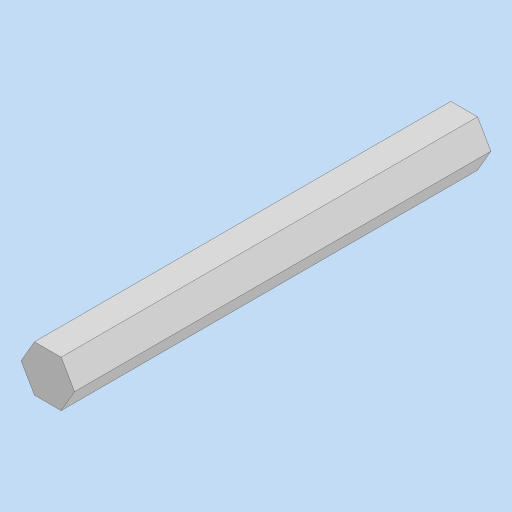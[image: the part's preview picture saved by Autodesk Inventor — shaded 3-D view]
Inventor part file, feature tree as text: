
AUTODESK INVENTOR PART (.ipt)
format: ipt  version: 2023 (Build 270158000, 158)  size: 83,456 bytes
history: native  units: in
note: dims shown in document units (in); Inventor stores cm internally (conversion verified against a paired STEP export)
features: extrude x1, sketch x1
ambient origin geometry x8: Origin, YZ Plane, XZ Plane, XY Plane, X Axis, Y Axis, Z Axis, Center Point
bodies: Solid1 (feature_tree)
feature tree (2):
  extrude  "Extrusion1"  Depth=4.5in TaperAngle=0.0deg
  sketch  "Sketch1"  dims[d0=0.5in d1=4.5in d2=0.0in]
